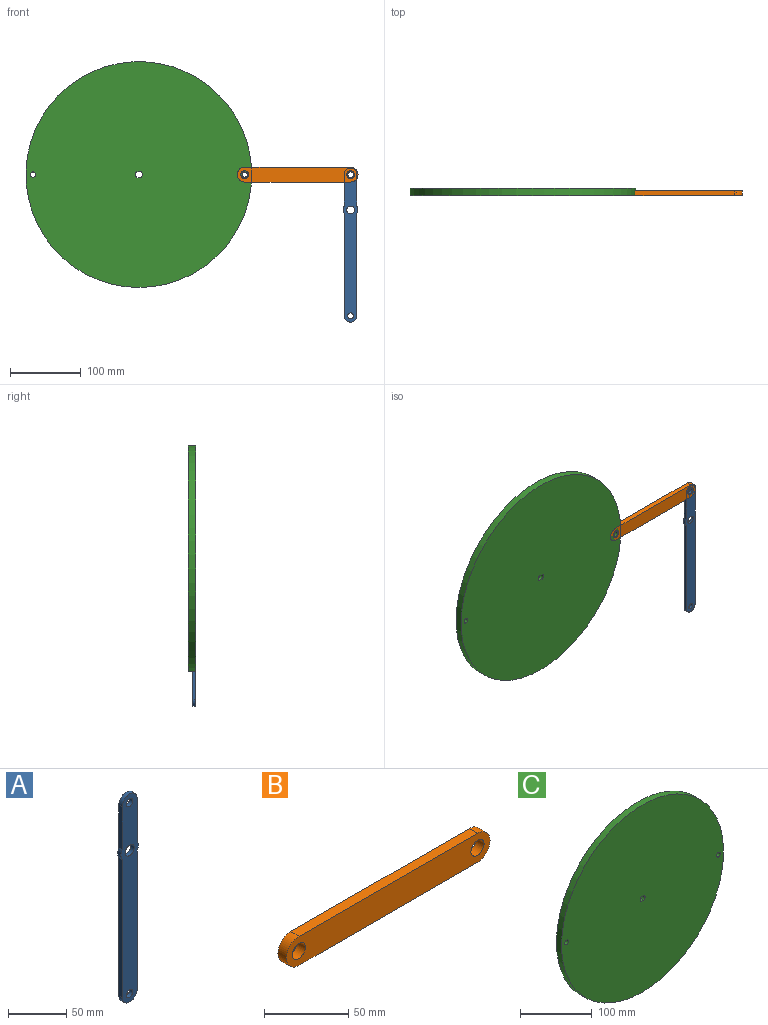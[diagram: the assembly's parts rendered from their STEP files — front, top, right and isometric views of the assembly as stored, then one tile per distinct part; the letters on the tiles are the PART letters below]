
ASSEMBLY  parts=3 mates=4
PART A: 13 faces, bbox 21x4x218 mm
  f0: plane 44.59x4mm, normal (-1,0,0), area 178.4mm2, adj f1,f10,f11,f12
  f1: cylinder r=10.5mm len=10.82mm, axis (0,-1,0), area 45.5mm2, adj f0,f2,f11,f12
  f2: plane 144.59x4mm, normal (-1,0,0), area 578.4mm2, adj f1,f3,f11,f12
  f3: cylinder r=9mm len=18mm, axis (0,-1,0), area 113.1mm2, adj f2,f4,f11,f12
  f4: plane 144.59x4mm, normal (1,0,0), area 578.4mm2, adj f3,f5,f11,f12
  f5: cylinder r=10.5mm len=10.82mm, axis (0,-1,0), area 45.5mm2, adj f4,f6,f11,f12
  f6: plane 44.59x4mm, normal (1,0,0), area 178.4mm2, adj f5,f10,f11,f12
  f7: cylinder r=4mm len=8mm, axis (0,-1,0), area 100.5mm2, adj f11,f12
  f8: cylinder r=5.5mm len=11mm, axis (0,-1,0), area 138.2mm2, adj f11,f12
  f9: cylinder r=4mm len=8mm, axis (0,-1,0), area 100.5mm2, adj f11,f12
  f10: cylinder r=9mm len=18mm, axis (0,-1,0), area 113.1mm2, adj f0,f6,f11,f12
  f11: plane 218x21mm, normal (0,1,0), area 3680.9mm2, adj f0,f1,f2,f3,f4,f5,f6,f7
  f12: plane 218x21mm, normal (0,-1,0), area 3680.9mm2, adj f0,f1,f2,f3,f4,f5,f6,f7
PART B: 8 faces, bbox 171x7x21 mm
  f0: plane 150x7mm, normal (0,0,-1), area 1050mm2, adj f1,f5,f6,f7
  f1: cylinder r=10.5mm len=21mm, axis (0,1,0), area 230.3mm2, adj f0,f2,f6,f7
  f2: plane 149.74x7mm, normal (0,0,1), area 1048.2mm2, adj f1,f5,f6,f7
  f3: cylinder r=5.5mm len=11mm, axis (0,1,0), area 241.9mm2, adj f6,f7
  f4: cylinder r=5.5mm len=11mm, axis (0,1,0), area 241.9mm2, adj f6,f7
  f5: cylinder r=10.5mm len=21mm, axis (0,1,0), area 233.3mm2, adj f0,f2,f6,f7
  f6: plane 171x21mm, normal (0,-1,0), area 3306mm2, adj f0,f1,f2,f3,f4,f5
  f7: plane 171x21mm, normal (0,1,0), area 3306mm2, adj f0,f1,f2,f3,f4,f5
PART C: 9 faces, bbox 320x10x320 mm
  f0: cylinder r=5mm len=10mm, axis (0,-1,0), area 97.9mm2, adj f1,f5,f7,f8
  f1: plane 10x5.58mm, normal (0,0,-1), area 55.8mm2, adj f0,f2,f7,f8
  f2: cylinder r=5mm len=10mm, axis (0,-1,0), area 97.9mm2, adj f1,f5,f7,f8
  f3: cylinder r=3.75mm len=10mm, axis (0,-1,0), area 235.6mm2, adj f7,f8
  f4: cylinder r=3.75mm len=10mm, axis (0,-1,0), area 235.6mm2, adj f7,f8
  f5: plane 10x5.58mm, normal (0,0,1), area 55.8mm2, adj f0,f2,f7,f8
  f6: cylinder r=160mm len=320mm, axis (0,-1,0), area 10053.1mm2, adj f7,f8
  f7: plane 320x320mm, normal (0,1,0), area 80264.3mm2, adj f0,f1,f2,f3,f4,f5,f6
  f8: plane 320x320mm, normal (0,-1,0), area 80264.3mm2, adj f0,f1,f2,f3,f4,f5,f6
PLACE A t=(96.06,-2,26.88)mm
PLACE B t=(96.02,5,26.88)mm
PLACE C t=(-3.94,-2,26.88)mm
MATE cylindrical B.f1 <-> A.f10  axis (0,-1,0) through (296.06,-2,26.88)mm
MATE cylindrical B.f3 <-> C.f3  axis (0,-1,0) through (146.06,-2,26.88)mm
MATE parallel C.f6 <-> A.f12  axis (0,-1,0) through (-3.94,-2,26.88)mm
MATE pin_slot C.f3 <-> B.f3  axis (0,-1,0) through (146.06,-2,26.88)mm
